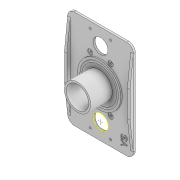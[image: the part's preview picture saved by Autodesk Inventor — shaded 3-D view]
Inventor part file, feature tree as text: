
AUTODESK INVENTOR PART (.ipt)
format: ipt  version: 2020.3 (Build 243373000, 373)  size: 269,824 bytes
history: native  units: mm
features: sketch x3, extrude x2, imported_body x1
ambient origin geometry x8: Origin, YZ Plane, XZ Plane, XY Plane, X Axis, Y Axis, Z Axis, Center Point
bodies: Solid1 (feature_tree)
feature tree (6):
  extrude  "Extrusion1"  Depth=1.0mm TaperAngle=0.0deg
  extrude  "Extrusion2"  [1 undecoded]
  sketch  "Sketch3"
  sketch  "Sketch1"  dims[d0=1.0mm d1=0.0mm d2=1.0mm d3=0.0mm]
  sketch  "Sketch2"
  imported_body  "Base1"
note: 1 required parameter value undecoded (feature->parameter linkage not recoverable at this tier; creation-order binding heuristic only, values carry confidence <= 0.55)
